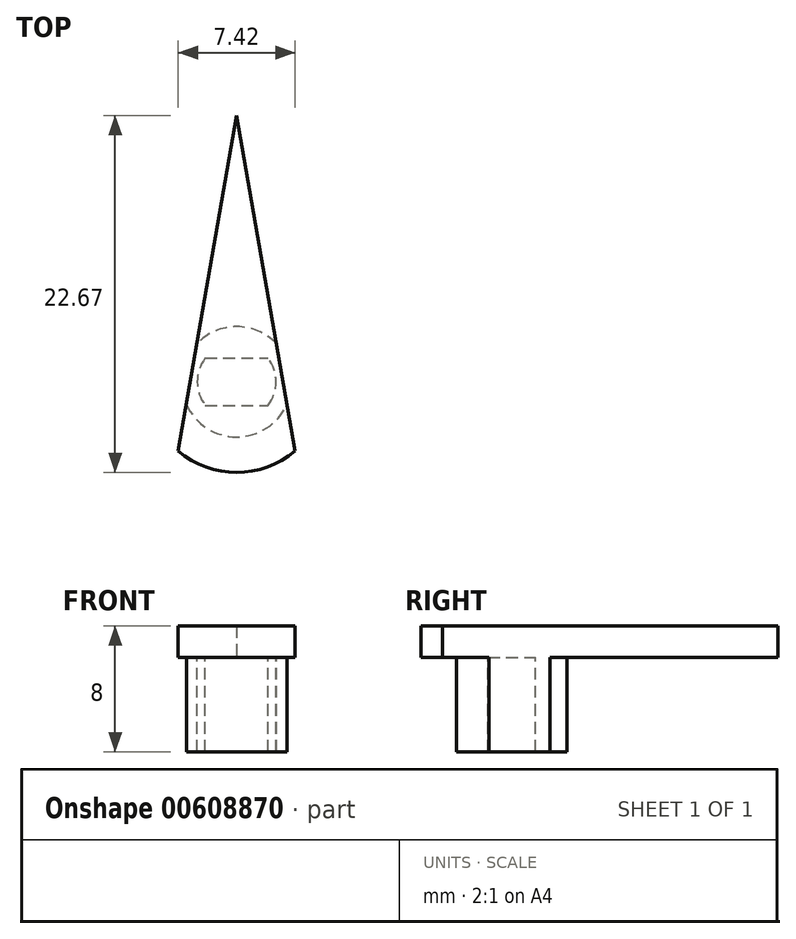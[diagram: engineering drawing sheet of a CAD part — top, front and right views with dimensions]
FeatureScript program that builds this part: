
annotation { "Feature Type Name" : "Feature", "Feature Type Description" : "" }
export const myFeature = defineFeature(function(context is Context, id is Id, definition is map)
    precondition{}
    {
        {
            var Q0;
            Q0=qCreatedBy(makeId("Top.planeOp"),FACE);
            var sketch = newSketch(context, id + "F0", { "sketchPlane" : qUnion([Q0])});
            skCircle(sketch, "E0", {"center": v(0, 0) * mm, "radius": 2.5 * mm});
            skLineSegment(sketch, "E1", {"start": v(-2, 1.5) * mm, "end": v(2, 1.5) * mm});
            skLineSegment(sketch, "E2.MirrorCS", {"start": v(-2, -1.5) * mm, "end": v(2, -1.5) * mm});
            skLineSegment(sketch, "E3", {"start": v(-3.71, -4.4) * mm, "end": v(0, 16.9) * mm});
            skLineSegment(sketch, "E4.MirrorCS", {"start": v(3.71, -4.4) * mm, "end": v(0, 16.9) * mm});
            skArc(sketch, "E5", {"start": v(-3.71, -4.4) * mm, "mid": v(0, -5.76) * mm, "end": v(3.71, -4.4) * mm});
            skCircle(sketch, "E6", {"center": v(0, 0) * mm, "radius": 3.5 * mm});
            skSolve(sketch);
        }
        {
            var Q0;
            {var subQ0=sQuery(id+"F0.wireOp",EDGE,"E1");Q0=makeQuery(id+"F0.imprint","IMPRINT",FACE,{"disambiguationData":[TD([[makeQuery(id+"F0.imprint","IMPRINT",EDGE,{"derivedFrom":subQ0}),1.0]])]});}
            var Q1;
            {var subQ0=sQuery(id+"F0.wireOp",EDGE,"E2.MirrorCS");Q1=makeQuery(id+"F0.imprint","IMPRINT",FACE,{"disambiguationData":[TD([[makeQuery(id+"F0.imprint","IMPRINT",EDGE,{"derivedFrom":subQ0}),-1.0]])]});}
            var Q2;
            Q2=makeQuery(id+"F0.imprint","IMPRINT",FACE,{"disambiguationData":[TD([[makeQuery(id+"F0.imprint","IMPRINT",EDGE,{"derivedFrom":sQuery(id+"F0.wireOp",EDGE,"E3")}),-1.0]])]});
            var Q3;
            {var subQ0=sQuery(id+"F0.wireOp",EDGE,"E1");Q3=makeQuery(id+"F0.imprint","IMPRINT",FACE,{"disambiguationData":[TD([[makeQuery(id+"F0.imprint","IMPRINT",EDGE,{"derivedFrom":subQ0}),-1.0]])]});}
            var Q4;
            {var subQ0=sQuery(id+"F0.wireOp",EDGE,"E6");var subQ1=sQuery(id+"F0.wireOp",EDGE,"E4.MirrorCS");var subQ2=makeQuery(id+"F0.imprint","INTERSECT",VERTEX,{"disambiguationData":[OD(0.0)],"derivedFrom":[subQ1,subQ0]});Q4=makeQuery(id+"F0.imprint","IMPRINT",FACE,{"disambiguationData":[TD([[makeQuery(id+"F0.imprint","IMPRINT",EDGE,{"disambiguationData":[TD([[subQ2,-1.0]])],"derivedFrom":subQ1}),-1.0]])]});}
            var Q5;
            {var subQ0=sQuery(id+"F0.wireOp",EDGE,"E1");var subQ1=sQuery(id+"F0.wireOp",EDGE,"E0");var subQ11=makeQuery(id+"F0.imprint","INTERSECT",VERTEX,{"disambiguationData":[OD(0.0)],"derivedFrom":[subQ1,subQ0]});Q5=makeQuery(id+"F0.imprint","IMPRINT",FACE,{"disambiguationData":[TD([[makeQuery(id+"F0.imprint","IMPRINT",EDGE,{"disambiguationData":[TD([[subQ11,1.0]])],"derivedFrom":subQ1}),-1.0]])]});}
            var Q6;
            {var subQ0=sQuery(id+"F0.wireOp",EDGE,"E5");Q6=makeQuery(id+"F0.imprint","IMPRINT",FACE,{"disambiguationData":[TD([[makeQuery(id+"F0.imprint","IMPRINT",EDGE,{"derivedFrom":subQ0}),1.0]])]});}
            var Q7;
            {var subQ0=sQuery(id+"F0.wireOp",EDGE,"E6");var subQ1=sQuery(id+"F0.wireOp",EDGE,"E3");var subQ2=makeQuery(id+"F0.imprint","INTERSECT",VERTEX,{"disambiguationData":[OD(0.0)],"derivedFrom":[subQ1,subQ0]});Q7=makeQuery(id+"F0.imprint","IMPRINT",FACE,{"disambiguationData":[TD([[makeQuery(id+"F0.imprint","IMPRINT",EDGE,{"disambiguationData":[TD([[subQ2,-1.0]])],"derivedFrom":subQ1}),1.0]])]});}
            extrude(context, id + "F1", {"entities" : qUnion([Q0, Q1, Q2, Q3, Q4, Q5, Q6, Q7]), "depth" : 2 * mm, "offsetDistance" : 25 * mm});
        }
        {
            var Q0;
            {var subQ0=sQuery(id+"F0.wireOp",EDGE,"E6");var subQ1=sQuery(id+"F0.wireOp",EDGE,"E3");var subQ2=makeQuery(id+"F0.imprint","INTERSECT",VERTEX,{"disambiguationData":[OD(0.0)],"derivedFrom":[subQ1,subQ0]});Q0=makeQuery(id+"F0.imprint","IMPRINT",FACE,{"disambiguationData":[TD([[makeQuery(id+"F0.imprint","IMPRINT",EDGE,{"disambiguationData":[TD([[subQ2,-1.0]])],"derivedFrom":subQ1}),1.0]])]});}
            var Q1;
            {var subQ0=sQuery(id+"F0.wireOp",EDGE,"E6");var subQ1=sQuery(id+"F0.wireOp",EDGE,"E4.MirrorCS");var subQ2=makeQuery(id+"F0.imprint","INTERSECT",VERTEX,{"disambiguationData":[OD(0.0)],"derivedFrom":[subQ1,subQ0]});Q1=makeQuery(id+"F0.imprint","IMPRINT",FACE,{"disambiguationData":[TD([[makeQuery(id+"F0.imprint","IMPRINT",EDGE,{"disambiguationData":[TD([[subQ2,-1.0]])],"derivedFrom":subQ1}),-1.0]])]});}
            var Q2;
            {var subQ0=sQuery(id+"F0.wireOp",EDGE,"E1");var subQ1=sQuery(id+"F0.wireOp",EDGE,"E0");var subQ11=makeQuery(id+"F0.imprint","INTERSECT",VERTEX,{"disambiguationData":[OD(0.0)],"derivedFrom":[subQ1,subQ0]});Q2=makeQuery(id+"F0.imprint","IMPRINT",FACE,{"disambiguationData":[TD([[makeQuery(id+"F0.imprint","IMPRINT",EDGE,{"disambiguationData":[TD([[subQ11,1.0]])],"derivedFrom":subQ1}),-1.0]])]});}
            var Q3;
            {var subQ0=sQuery(id+"F0.wireOp",EDGE,"E1");Q3=makeQuery(id+"F0.imprint","IMPRINT",FACE,{"disambiguationData":[TD([[makeQuery(id+"F0.imprint","IMPRINT",EDGE,{"derivedFrom":subQ0}),1.0]])]});}
            var Q4;
            {var subQ0=sQuery(id+"F0.wireOp",EDGE,"E2.MirrorCS");Q4=makeQuery(id+"F0.imprint","IMPRINT",FACE,{"disambiguationData":[TD([[makeQuery(id+"F0.imprint","IMPRINT",EDGE,{"derivedFrom":subQ0}),-1.0]])]});}
            extrude(context, id + "F2", {"entities" : qUnion([Q0, Q1, Q2, Q3, Q4]), "operationType" : NewBodyOperationType.ADD, "oppositeDirection" : true, "depth" : 6 * mm, "offsetDistance" : 25 * mm});
        }
    });
